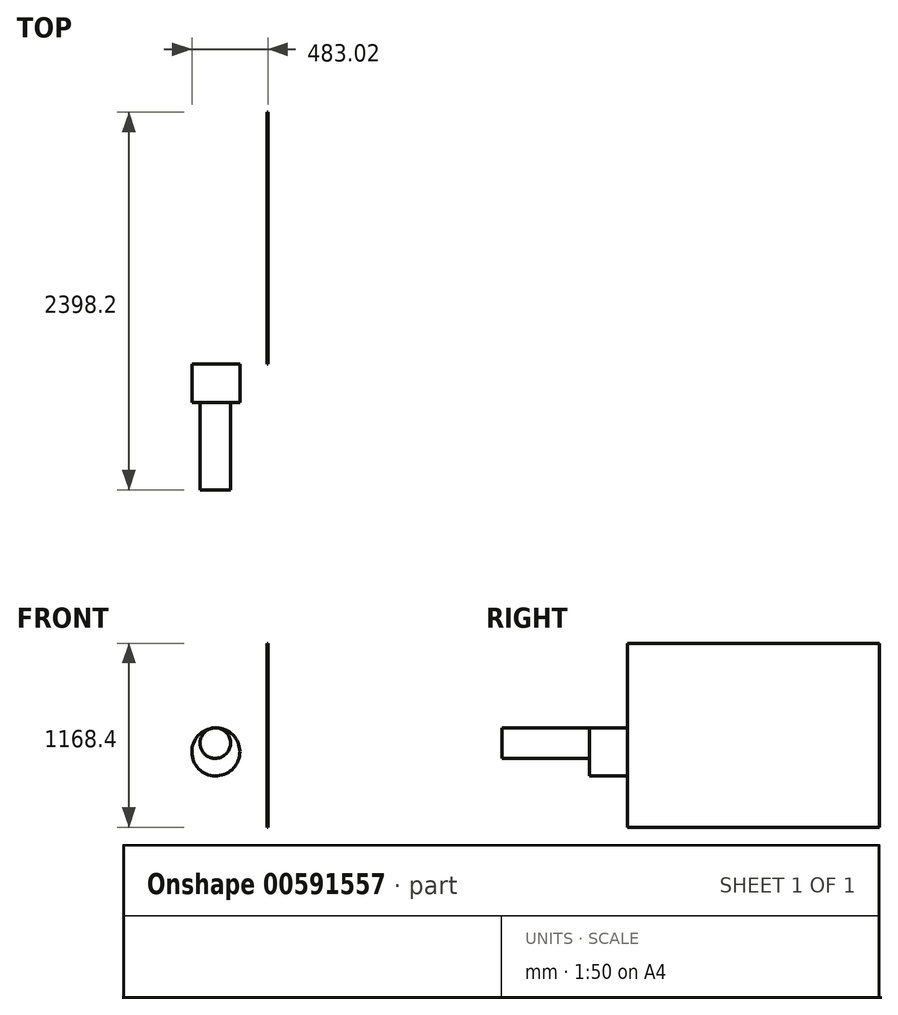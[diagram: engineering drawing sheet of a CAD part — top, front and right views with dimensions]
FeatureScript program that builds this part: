
annotation { "Feature Type Name" : "Feature", "Feature Type Description" : "" }
export const myFeature = defineFeature(function(context is Context, id is Id, definition is map)
    precondition{}
    {
        {
            var Q0;
            Q0=qCreatedBy(makeId("Right.planeOp"),FACE);
            var sketch = newSketch(context, id + "F0", { "sketchPlane" : qUnion([Q0])});
            skLineSegment(sketch, "E0.bottom", {"start": v(0, 0) * mm, "end": v(1600.2, 0) * mm});
            skLineSegment(sketch, "E0.top", {"start": v(0, 1168.4) * mm, "end": v(1600.2, 1168.4) * mm});
            skLineSegment(sketch, "E0.left", {"start": v(0, 0) * mm, "end": v(0, 1168.4) * mm});
            skLineSegment(sketch, "E0.right", {"start": v(1600.2, 0) * mm, "end": v(1600.2, 1168.4) * mm});
            skSolve(sketch);
        }
        {
            var Q0;
            Q0=qCreatedBy(makeId("Front.planeOp"),FACE);
            var sketch = newSketch(context, id + "F1", { "sketchPlane" : qUnion([Q0])});
            skCircle(sketch, "E1", {"center": v(-325.52, 478.72) * mm, "radius": 152.5 * mm});
            skSolve(sketch);
        }
        {
            var Q0;
            Q0 = qSketchRegion(id + "F1", true);
            extrude(context, id + "F2", {"entities" : qUnion([Q0]), "depth" : 243 * mm, "offsetDistance" : 25 * mm});
        }
        {
            var Q0;
            Q0=makeQuery(id+"F2.opExtrude","CAP_FACE",FACE,{"disambiguationData":[OSD([sQuery(id+"F1.wireOp",EDGE,"E1")])],"isStart":false});
            var sketch = newSketch(context, id + "F3", { "sketchPlane" : qUnion([Q0])});
            skLineSegment(sketch, "E2", {"start": v(-329, 631.18) * mm, "end": v(-324.58, 437.53) * mm, "construction": true});
            skCircle(sketch, "E3", {"center": v(-329.2, 534.43) * mm, "radius": 97.01 * mm});
            skPoint(sketch, "E3.first.point", {"position": v(-322.04, 631.18) * mm});
            skPoint(sketch, "E3.third.point", {"position": v(-236.74, 505.02) * mm});
            skSolve(sketch);
        }
        {
            var Q0;
            Q0 = qSketchRegion(id + "F3", true);
            extrude(context, id + "F4", {"entities" : qUnion([Q0]), "operationType" : NewBodyOperationType.ADD, "depth" : 555 * mm, "offsetDistance" : 25 * mm});
        }
        {
            var Q0;
            Q0=makeQuery(id+"F0.imprint","IMPRINT",FACE,{"disambiguationData":[TD([[makeQuery(id+"F0.imprint","IMPRINT",EDGE,{"derivedFrom":sQuery(id+"F0.wireOp",EDGE,"E0.bottom")}),1.0]])]});
            extrude(context, id + "F5", {"entities" : qUnion([Q0]), "depth" : 5 * mm, "offsetDistance" : 25 * mm});
        }
    });
